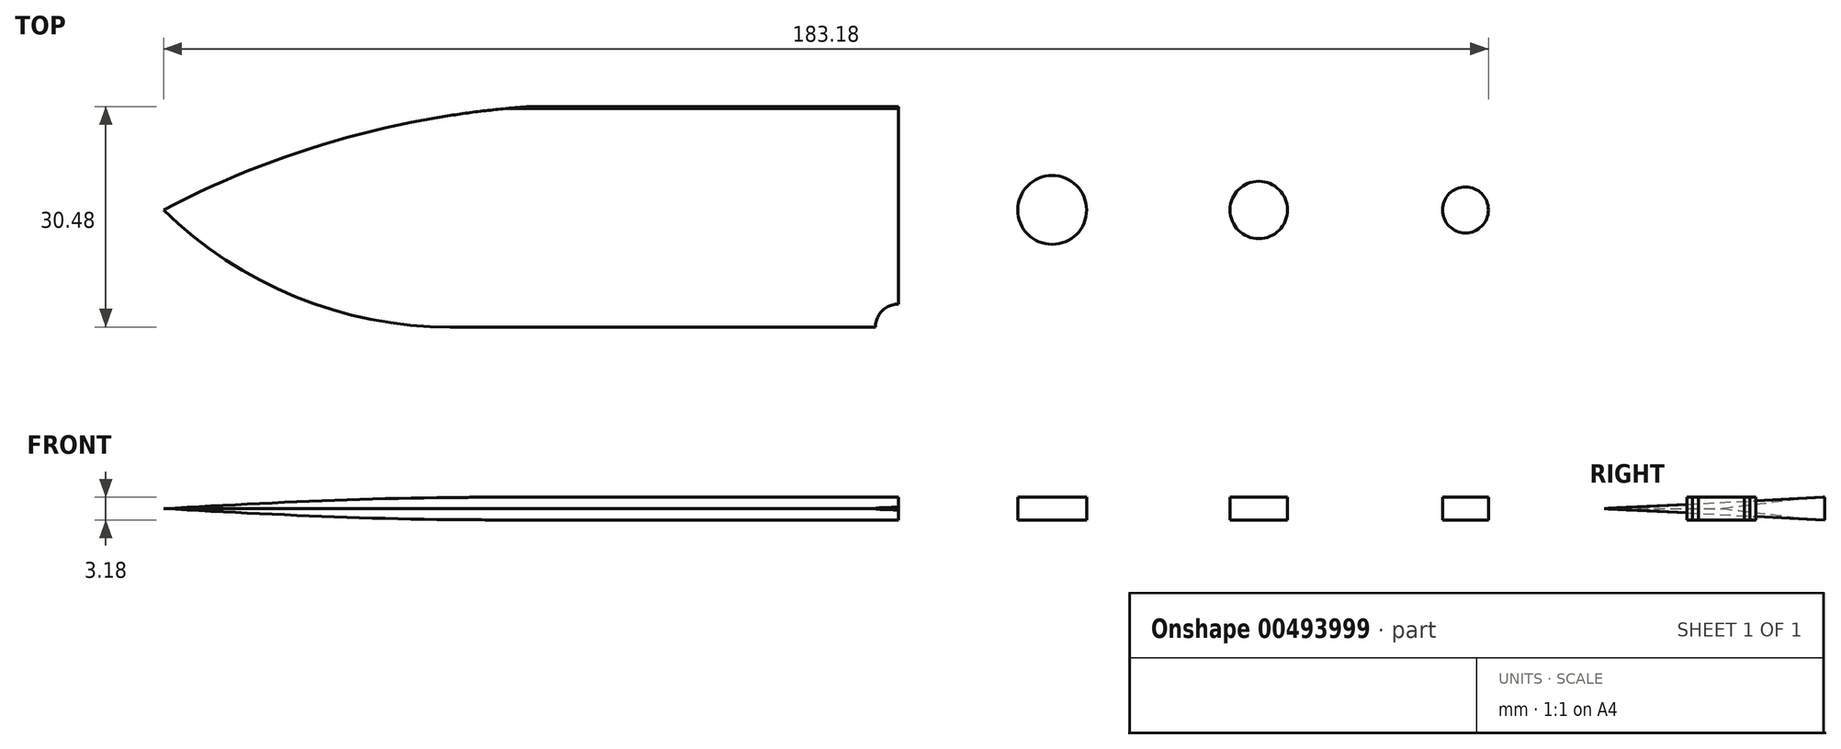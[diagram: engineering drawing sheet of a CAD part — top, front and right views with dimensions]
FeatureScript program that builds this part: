
annotation { "Feature Type Name" : "Feature", "Feature Type Description" : "" }
export const myFeature = defineFeature(function(context is Context, id is Id, definition is map)
    precondition{}
    {
        {
            var Q0;
            Q0=qCreatedBy(makeId("Top.planeOp"),FACE);
            var sketch = newSketch(context, id + "F0", { "sketchPlane" : qUnion([Q0])});
            skLineSegment(sketch, "E0", {"start": v(0, 0) * mm, "end": v(203.2, 0) * mm});
            skLineSegment(sketch, "E1", {"start": v(203.2, 0) * mm, "end": v(203.2, -38.1) * mm});
            skLineSegment(sketch, "E2", {"start": v(203.2, -38.1) * mm, "end": v(0, -38.1) * mm});
            skLineSegment(sketch, "E3", {"start": v(0, -38.1) * mm, "end": v(0, 0) * mm});
            skSolve(sketch);
        }
        {
            var Q0;
            Q0 = qSketchRegion(id + "F0", true);
            extrude(context, id + "F1", {"entities" : qUnion([Q0]), "depth" : 3.17 * mm});
        }
        {
            var Q0;
            Q0=makeQuery(id+"F1.opExtrude","CAP_FACE",FACE,{"disambiguationData":[OSD([sQuery(id+"F0.wireOp",EDGE,"E0"),sQuery(id+"F0.wireOp",EDGE,"E1"),sQuery(id+"F0.wireOp",EDGE,"E2"),sQuery(id+"F0.wireOp",EDGE,"E3")])],"isStart":false});
            var sketch = newSketch(context, id + "F2", { "sketchPlane" : qUnion([Q0])});
            skLineSegment(sketch, "E4", {"start": v(101.6, 0) * mm, "end": v(101.6, -38.1) * mm});
            skLineSegment(sketch, "E5", {"start": v(0, 0) * mm, "end": v(0, -19.05) * mm});
            skLineSegment(sketch, "E6", {"start": v(0, -9.53) * mm, "end": v(0, -19.05) * mm});
            skLineSegment(sketch, "E7", {"start": v(0, 0) * mm, "end": v(101.6, 0) * mm});
            skLineSegment(sketch, "E8", {"start": v(39.6, -30.48) * mm, "end": v(101.6, -30.48) * mm});
            skArc(sketch, "E9", {"start": v(50.8, 0) * mm, "mid": v(24.65, -4.48) * mm, "end": v(0, -14.29) * mm});
            skCircle(sketch, "E10", {"center": v(101.6, -30.48) * mm, "radius": 3.18 * mm});
            skLineSegment(sketch, "E11", {"start": v(101.6, -30.48) * mm, "end": v(126.72, -30.48) * mm});
            skLineSegment(sketch, "E12", {"start": v(101.6, -33.65) * mm, "end": v(126.77, -33.65) * mm});
            skLineSegment(sketch, "E13", {"start": v(104.78, -30.48) * mm, "end": v(104.78, -33.65) * mm});
            skLineSegment(sketch, "E14", {"start": v(104.78, -33.65) * mm, "end": v(104.78, -38.1) * mm});
            skArc(sketch, "E15", {"start": v(134.38, -28.16) * mm, "mid": v(118.68, -26.05) * mm, "end": v(104.78, -33.66) * mm});
            skLineSegment(sketch, "E16", {"start": v(203.2, 0) * mm, "end": v(203.2, -19.05) * mm});
            skArc(sketch, "E17", {"start": v(193.68, -26.2) * mm, "mid": v(163.91, -23.67) * mm, "end": v(134.38, -28.16) * mm});
            skPoint(sketch, "E18", {"position": v(39.6, -30.48) * mm});
            skArc(sketch, "E19", {"start": v(0, -14.29) * mm, "mid": v(18.2, -26.28) * mm, "end": v(39.6, -30.48) * mm});
            skLineSegment(sketch, "E20", {"start": v(0, -14.29) * mm, "end": v(203.2, -14.29) * mm});
            skLineSegment(sketch, "E21", {"start": v(184.15, 0) * mm, "end": v(203.2, -14.29) * mm});
            skLineSegment(sketch, "E22", {"start": v(203.2, -14.29) * mm, "end": v(184.15, -38.1) * mm});
            skCircle(sketch, "E23", {"center": v(122.86, -14.29) * mm, "radius": 4.76 * mm});
            skCircle(sketch, "E24", {"center": v(180, -14.29) * mm, "radius": 3.18 * mm});
            skCircle(sketch, "E25", {"center": v(151.43, -14.29) * mm, "radius": 3.97 * mm});
            skSolve(sketch);
        }
        {
            var Q0;
            {var subQ0=sQuery(id+"F2.wireOp",EDGE,"E5");Q0=makeQuery(id+"F2.imprint","IMPRINT",FACE,{"disambiguationData":[TD([[makeQuery(id+"F2.imprint","IMPRINT",EDGE,{"derivedFrom":subQ0}),-1.0]])]});}
            var Q1;
            {var subQ0=sQuery(id+"F2.wireOp",EDGE,"hBmztbTj-tqe3-CgKz-6O3F-K7U5qk9btVsn");var subQ1=sQuery(id+"F2.wireOp",EDGE,"E8");var subQ2=makeQuery(id+"F2.imprint","INTERSECT",VERTEX,{"derivedFrom":[subQ1,subQ0]});Q1=makeQuery(id+"F2.imprint","IMPRINT",FACE,{"disambiguationData":[TD([[makeQuery(id+"F2.imprint","IMPRINT",EDGE,{"disambiguationData":[TD([[subQ2,-1.0]])],"derivedFrom":subQ1}),-1.0]])]});}
            var Q2;
            {var subQ5=sQuery(id+"F2.wireOp",EDGE,"E14");Q2=makeQuery(id+"F2.imprint","IMPRINT",FACE,{"disambiguationData":[TD([[makeQuery(id+"F2.imprint","IMPRINT",EDGE,{"derivedFrom":subQ5}),-1.0]])]});}
            var Q3;
            {var subQ3=sQuery(id+"F2.wireOp",EDGE,"E13");Q3=makeQuery(id+"F2.imprint","IMPRINT",FACE,{"disambiguationData":[TD([[makeQuery(id+"F2.imprint","IMPRINT",EDGE,{"derivedFrom":subQ3}),-1.0]])]});}
            var Q4;
            {var subQ0=sQuery(id+"F2.wireOp",EDGE,"E11");var subQ1=sQuery(id+"F2.wireOp",EDGE,"E4");var subQ2=makeQuery(id+"F2.imprint","INTERSECT",VERTEX,{"derivedFrom":[subQ1,sQuery(id+"F2.wireOp",EDGE,"E8"),subQ0]});Q4=makeQuery(id+"F2.imprint","IMPRINT",FACE,{"disambiguationData":[TD([[makeQuery(id+"F2.imprint","IMPRINT",EDGE,{"disambiguationData":[TD([[subQ2,-1.0]])],"derivedFrom":subQ1}),1.0]])]});}
            var Q5;
            {var subQ1=sQuery(id+"F2.wireOp",EDGE,"E4");var subQ3=sQuery(id+"F2.wireOp",EDGE,"E10");var subQ4=makeQuery(id+"F2.imprint","INTERSECT",VERTEX,{"derivedFrom":[subQ1,subQ3]});Q5=makeQuery(id+"F2.imprint","IMPRINT",FACE,{"disambiguationData":[TD([[makeQuery(id+"F2.imprint","IMPRINT",EDGE,{"disambiguationData":[TD([[subQ4,-1.0]])],"derivedFrom":subQ1}),1.0]])]});}
            var Q6;
            {var subQ1=sQuery(id+"F2.wireOp",EDGE,"E4");var subQ3=sQuery(id+"F2.wireOp",EDGE,"E10");var subQ4=makeQuery(id+"F2.imprint","INTERSECT",VERTEX,{"derivedFrom":[subQ1,subQ3]});Q6=makeQuery(id+"F2.imprint","IMPRINT",FACE,{"disambiguationData":[TD([[makeQuery(id+"F2.imprint","IMPRINT",EDGE,{"disambiguationData":[TD([[subQ4,-1.0]])],"derivedFrom":subQ3}),1.0]])]});}
            var Q7;
            {var subQ0=sQuery(id+"F2.wireOp",EDGE,"E8");var subQ3=sQuery(id+"F2.wireOp",EDGE,"E10");var subQ5=makeQuery(id+"F2.imprint","INTERSECT",VERTEX,{"derivedFrom":[subQ0,subQ3]});Q7=makeQuery(id+"F2.imprint","IMPRINT",FACE,{"disambiguationData":[TD([[makeQuery(id+"F2.imprint","IMPRINT",EDGE,{"disambiguationData":[TD([[subQ5,-1.0]])],"derivedFrom":subQ0}),-1.0]])]});}
            var Q8;
            {var subQ1=sQuery(id+"F2.wireOp",EDGE,"E14");Q8=makeQuery(id+"F2.imprint","IMPRINT",FACE,{"disambiguationData":[TD([[makeQuery(id+"F2.imprint","IMPRINT",EDGE,{"derivedFrom":subQ1}),1.0]])]});}
            var Q9;
            {var subQ0=sQuery(id+"F2.wireOp",EDGE,"locTSA2M-AsP4-2HM6-qX5g-so1iKQziUQEc");var subQ4=makeQuery(id+"F2.imprint","INTERSECT",VERTEX,{"derivedFrom":[subQ0,sQuery(id+"F2.wireOp",EDGE,"E17")]});Q9=makeQuery(id+"F2.imprint","IMPRINT",FACE,{"disambiguationData":[TD([[makeQuery(id+"F2.imprint","IMPRINT",EDGE,{"disambiguationData":[TD([[subQ4,-1.0]])],"derivedFrom":subQ0}),1.0]])]});}
            var Q10;
            {var subQ0=sQuery(id+"F2.wireOp",EDGE,"locTSA2M-AsP4-2HM6-qX5g-so1iKQziUQEc");var subQ3=sQuery(id+"F2.wireOp",EDGE,"E17");var subQ5=makeQuery(id+"F2.imprint","INTERSECT",VERTEX,{"derivedFrom":[subQ0,subQ3]});Q10=makeQuery(id+"F2.imprint","IMPRINT",FACE,{"disambiguationData":[TD([[makeQuery(id+"F2.imprint","IMPRINT",EDGE,{"disambiguationData":[TD([[subQ5,-1.0]])],"derivedFrom":subQ3}),1.0]])]});}
            var Q11;
            {var subQ1=sQuery(id+"F2.wireOp",EDGE,"pldBipSu-5jdq-XlzJ-CgNP-Urclp5KgjKv2");var subQ3=sQuery(id+"F2.wireOp",EDGE,"hBmztbTj-tqe3-CgKz-6O3F-K7U5qk9btVsn");var subQ4=makeQuery(id+"F2.imprint","INTERSECT",VERTEX,{"derivedFrom":[subQ1,subQ3]});Q11=makeQuery(id+"F2.imprint","IMPRINT",FACE,{"disambiguationData":[TD([[makeQuery(id+"F2.imprint","IMPRINT",EDGE,{"disambiguationData":[TD([[subQ4,1.0]])],"derivedFrom":subQ1}),1.0]])]});}
            var Q12;
            {var subQ3=sQuery(id+"F2.wireOp",EDGE,"E8");var subQ9=sQuery(id+"F2.wireOp",EDGE,"E19");var subQ10=makeQuery(id+"F2.imprint","INTERSECT",VERTEX,{"derivedFrom":[subQ3,subQ9]});Q12=makeQuery(id+"F2.imprint","IMPRINT",FACE,{"disambiguationData":[TD([[makeQuery(id+"F2.imprint","IMPRINT",EDGE,{"disambiguationData":[TD([[subQ10,-1.0]])],"derivedFrom":subQ3}),-1.0]])]});}
            var Q13;
            {var subQ0=sQuery(id+"F2.wireOp",EDGE,"E16");Q13=makeQuery(id+"F2.imprint","IMPRINT",FACE,{"disambiguationData":[TD([[makeQuery(id+"F2.imprint","IMPRINT",EDGE,{"derivedFrom":subQ0}),-1.0]])]});}
            var Q14;
            {var subQ5=sQuery(id+"F2.wireOp",EDGE,"E22");var subQ6=makeQuery(id+"F2.imprint","INTERSECT",VERTEX,{"derivedFrom":[sQuery(id+"F2.wireOp",EDGE,"E17"),subQ5]});Q14=makeQuery(id+"F2.imprint","IMPRINT",FACE,{"disambiguationData":[TD([[makeQuery(id+"F2.imprint","IMPRINT",EDGE,{"disambiguationData":[TD([[subQ6,-1.0]])],"derivedFrom":subQ5}),1.0]])]});}
            var Q15;
            {var subQ0=sQuery(id+"F2.wireOp",EDGE,"E13");Q15=makeQuery(id+"F2.imprint","IMPRINT",FACE,{"disambiguationData":[TD([[makeQuery(id+"F2.imprint","IMPRINT",EDGE,{"derivedFrom":subQ0}),1.0]])]});}
            var Q16;
            {var subQ0=sQuery(id+"F2.wireOp",EDGE,"E23");var subQ1=sQuery(id+"F2.wireOp",EDGE,"E20");var subQ2=makeQuery(id+"F2.imprint","INTERSECT",VERTEX,{"disambiguationData":[OD(0.0)],"derivedFrom":[subQ1,subQ0]});Q16=makeQuery(id+"F2.imprint","IMPRINT",FACE,{"disambiguationData":[TD([[makeQuery(id+"F2.imprint","IMPRINT",EDGE,{"disambiguationData":[TD([[subQ2,-1.0]])],"derivedFrom":subQ1}),1.0]])]});}
            var Q17;
            {var subQ0=sQuery(id+"F2.wireOp",EDGE,"E23");var subQ1=sQuery(id+"F2.wireOp",EDGE,"E20");var subQ2=makeQuery(id+"F2.imprint","INTERSECT",VERTEX,{"disambiguationData":[OD(0.0)],"derivedFrom":[subQ1,subQ0]});Q17=makeQuery(id+"F2.imprint","IMPRINT",FACE,{"disambiguationData":[TD([[makeQuery(id+"F2.imprint","IMPRINT",EDGE,{"disambiguationData":[TD([[subQ2,-1.0]])],"derivedFrom":subQ1}),-1.0]])]});}
            var Q18;
            {var subQ0=sQuery(id+"F2.wireOp",EDGE,"E24");var subQ1=sQuery(id+"F2.wireOp",EDGE,"E20");var subQ2=makeQuery(id+"F2.imprint","INTERSECT",VERTEX,{"disambiguationData":[OD(0.0)],"derivedFrom":[subQ1,subQ0]});Q18=makeQuery(id+"F2.imprint","IMPRINT",FACE,{"disambiguationData":[TD([[makeQuery(id+"F2.imprint","IMPRINT",EDGE,{"disambiguationData":[TD([[subQ2,-1.0]])],"derivedFrom":subQ1}),1.0]])]});}
            var Q19;
            {var subQ0=sQuery(id+"F2.wireOp",EDGE,"E24");var subQ1=sQuery(id+"F2.wireOp",EDGE,"E20");var subQ2=makeQuery(id+"F2.imprint","INTERSECT",VERTEX,{"disambiguationData":[OD(0.0)],"derivedFrom":[subQ1,subQ0]});Q19=makeQuery(id+"F2.imprint","IMPRINT",FACE,{"disambiguationData":[TD([[makeQuery(id+"F2.imprint","IMPRINT",EDGE,{"disambiguationData":[TD([[subQ2,-1.0]])],"derivedFrom":subQ1}),-1.0]])]});}
            var Q20;
            {var subQ0=sQuery(id+"F2.wireOp",EDGE,"E25");var subQ1=sQuery(id+"F2.wireOp",EDGE,"E20");var subQ2=makeQuery(id+"F2.imprint","INTERSECT",VERTEX,{"disambiguationData":[OD(0.0)],"derivedFrom":[subQ1,subQ0]});Q20=makeQuery(id+"F2.imprint","IMPRINT",FACE,{"disambiguationData":[TD([[makeQuery(id+"F2.imprint","IMPRINT",EDGE,{"disambiguationData":[TD([[subQ2,-1.0]])],"derivedFrom":subQ1}),1.0]])]});}
            var Q21;
            {var subQ0=sQuery(id+"F2.wireOp",EDGE,"E25");var subQ1=sQuery(id+"F2.wireOp",EDGE,"E20");var subQ2=makeQuery(id+"F2.imprint","INTERSECT",VERTEX,{"disambiguationData":[OD(0.0)],"derivedFrom":[subQ1,subQ0]});Q21=makeQuery(id+"F2.imprint","IMPRINT",FACE,{"disambiguationData":[TD([[makeQuery(id+"F2.imprint","IMPRINT",EDGE,{"disambiguationData":[TD([[subQ2,-1.0]])],"derivedFrom":subQ1}),-1.0]])]});}
            extrude(context, id + "F3", {"entities" : qUnion([Q0, Q1, Q2, Q3, Q4, Q5, Q6, Q7, Q8, Q9, Q10, Q11, Q12, Q13, Q14, Q15, Q16, Q17, Q18, Q19, Q20, Q21]), "operationType" : NewBodyOperationType.REMOVE, "oppositeDirection" : true, "depth" : 25.4 * mm});
        }
        {
            var Q0;
            {var subQ0=sQuery(id+"F2.wireOp",EDGE,"E19");Q0=makeQuery(id+"F2.imprint","IMPRINT",FACE,{"disambiguationData":[TD([[makeQuery(id+"F2.imprint","IMPRINT",EDGE,{"derivedFrom":subQ0}),1.0]])]});}
            cPlane(context, id + "F4", {"entities" : qUnion([Q0]), "cplaneType" : CPlaneType.OFFSET, "offset" : 1.59 * mm, "oppositeDirection" : true, "width" : 152.4 * mm, "height" : 152.4 * mm});
        }
        {
            var Q0;
            Q0=qCreatedBy(id+"F4.planeOp",FACE);
            var sketch = newSketch(context, id + "F5", { "sketchPlane" : qUnion([Q0])});
            skLineSegment(sketch, "E26", {"start": v(39.6, -30.48) * mm, "end": v(101.6, -30.48) * mm});
            skArc(sketch, "E27", {"start": v(0, -14.29) * mm, "mid": v(18.2, -26.28) * mm, "end": v(39.6, -30.48) * mm});
            skPoint(sketch, "E28", {"position": v(101.6, -30.48) * mm});
            skSolve(sketch);
        }
        {
            var Q0;
            Q0=qCreatedBy(makeId("Right.planeOp"),FACE);
            cPlane(context, id + "F6", {"entities" : qUnion([Q0]), "cplaneType" : CPlaneType.OFFSET, "offset" : 101.6 * mm, "width" : 152.4 * mm, "height" : 152.4 * mm});
        }
        {
            var Q0;
            Q0=qCreatedBy(id+"F6.planeOp",FACE);
            var sketch = newSketch(context, id + "F7", { "sketchPlane" : qUnion([Q0])});
            skLineSegment(sketch, "E29", {"start": v(0, 0) * mm, "end": v(-30.48, 0) * mm});
            skLineSegment(sketch, "E30", {"start": v(-30.48, 0) * mm, "end": v(-30.48, 1.59) * mm});
            skLineSegment(sketch, "E31", {"start": v(-30.48, 1.59) * mm, "end": v(0, 0) * mm});
            skLineSegment(sketch, "E32", {"start": v(-30.48, 1.59) * mm, "end": v(0, 3.19) * mm});
            skLineSegment(sketch, "E33", {"start": v(0, 3.19) * mm, "end": v(-30.48, 3.19) * mm});
            skLineSegment(sketch, "E34", {"start": v(-30.48, 3.19) * mm, "end": v(-30.48, 1.59) * mm});
            skLineSegment(sketch, "E35", {"start": v(-30.48, 1.59) * mm, "end": v(-3.22, 1.59) * mm});
            skLineSegment(sketch, "E36", {"start": v(-30.48, 1.59) * mm, "end": v(-4.12, 6.24) * mm});
            skLineSegment(sketch, "E37.MirrorCS", {"start": v(-30.48, 1.59) * mm, "end": v(-4.12, -3.06) * mm});
            skLineSegment(sketch, "E38", {"start": v(-4.12, -3.06) * mm, "end": v(-30.48, -3.06) * mm});
            skLineSegment(sketch, "E39", {"start": v(-30.48, -3.06) * mm, "end": v(-30.48, 1.59) * mm});
            skLineSegment(sketch, "E40", {"start": v(-4.12, 6.24) * mm, "end": v(-30.48, 6.24) * mm});
            skLineSegment(sketch, "E41", {"start": v(-30.48, 6.24) * mm, "end": v(-30.48, 1.59) * mm});
            skSolve(sketch);
        }
        {
            var Q0;
            Q0 = qSketchRegion(id + "F7", true);
            var Q1;
            Q1 = qConstructionFilter(qBodyType(qCreatedBy(id + "F5" ,EDGE), BodyType.WIRE), ConstructionObject.NO);
            sweep(context, id + "F8", {"operationType" : NewBodyOperationType.REMOVE, "profiles" : qUnion([Q0]), "path" : qUnion([Q1])});
        }
    });
